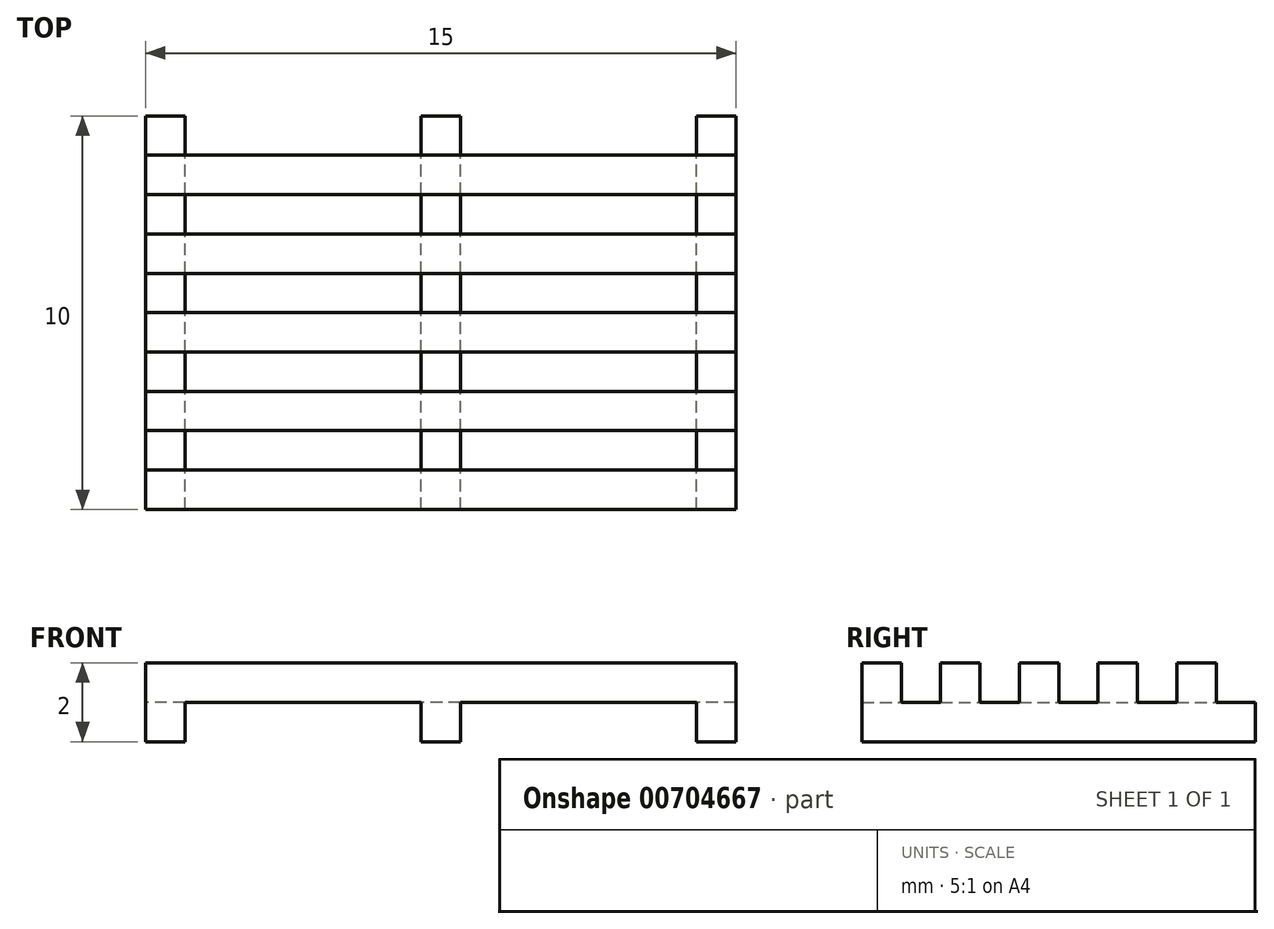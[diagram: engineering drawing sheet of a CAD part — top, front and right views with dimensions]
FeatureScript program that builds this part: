
annotation { "Feature Type Name" : "Feature", "Feature Type Description" : "" }
export const myFeature = defineFeature(function(context is Context, id is Id, definition is map)
    precondition{}
    {
        {
            var Q0;
            Q0=qCreatedBy(makeId("Top.planeOp"),FACE);
            var sketch = newSketch(context, id + "F0", { "sketchPlane" : qUnion([Q0])});
            skLineSegment(sketch, "E0.bottom", {"start": v(0, 0) * mm, "end": v(15, 0) * mm});
            skLineSegment(sketch, "E0.top", {"start": v(0, -10) * mm, "end": v(15, -10) * mm});
            skLineSegment(sketch, "E0.left", {"start": v(0, 0) * mm, "end": v(0, -10) * mm});
            skLineSegment(sketch, "E0.right", {"start": v(15, 0) * mm, "end": v(15, -10) * mm});
            skSolve(sketch);
        }
        {
            var Q0;
            Q0 = qSketchRegion(id + "F0", true);
            extrude(context, id + "F1", {"entities" : qUnion([Q0]), "depth" : 2 * mm, "offsetDistance" : 25 * mm});
        }
        {
            var Q0;
            Q0=qCreatedBy(makeId("Front.planeOp"),FACE);
            var sketch = newSketch(context, id + "F2", { "sketchPlane" : qUnion([Q0])});
            skLineSegment(sketch, "E1", {"start": v(1, 0) * mm, "end": v(1, 1) * mm});
            skLineSegment(sketch, "E2", {"start": v(1, 1) * mm, "end": v(7, 1) * mm});
            skLineSegment(sketch, "E3", {"start": v(7, 1) * mm, "end": v(7, 0) * mm});
            skLineSegment(sketch, "E4", {"start": v(8, 0) * mm, "end": v(8, 1) * mm});
            skLineSegment(sketch, "E5", {"start": v(8, 1) * mm, "end": v(14, 1) * mm});
            skLineSegment(sketch, "E6", {"start": v(14, 1) * mm, "end": v(14, 0) * mm});
            skLineSegment(sketch, "E7", {"start": v(14, 0) * mm, "end": v(8, 0) * mm});
            skLineSegment(sketch, "E8", {"start": v(7, 0) * mm, "end": v(1, 0) * mm});
            skSolve(sketch);
        }
        {
            var Q0;
            Q0 = qSketchRegion(id + "F2", true);
            extrude(context, id + "F3", {"entities" : qUnion([Q0]), "operationType" : NewBodyOperationType.REMOVE, "depth" : 25 * mm, "offsetDistance" : 25 * mm});
        }
        {
            var Q0;
            Q0=makeQuery(id+"F1.opExtrude","SWEPT_FACE",FACE,{"disambiguationData":[OSD([sQuery(id+"F0.wireOp",EDGE,"E0.left")])]});
            var sketch = newSketch(context, id + "F4", { "sketchPlane" : qUnion([Q0])});
            skLineSegment(sketch, "E9", {"start": v(0, 2.24) * mm, "end": v(0, 1) * mm});
            skLineSegment(sketch, "E10", {"start": v(0, 1) * mm, "end": v(1, 1) * mm});
            skLineSegment(sketch, "E11", {"start": v(1, 1) * mm, "end": v(1, 2) * mm});
            skLineSegment(sketch, "E12", {"start": v(1, 2) * mm, "end": v(2, 2) * mm});
            skLineSegment(sketch, "E13", {"start": v(2, 2) * mm, "end": v(2, 1) * mm});
            skLineSegment(sketch, "E14", {"start": v(2, 1) * mm, "end": v(3, 1) * mm});
            skLineSegment(sketch, "E15", {"start": v(3, 1) * mm, "end": v(3, 2) * mm});
            skLineSegment(sketch, "E16", {"start": v(3, 2) * mm, "end": v(4, 2) * mm});
            skLineSegment(sketch, "E17", {"start": v(4, 2) * mm, "end": v(4, 1) * mm});
            skLineSegment(sketch, "E18", {"start": v(4, 1) * mm, "end": v(5, 1) * mm});
            skLineSegment(sketch, "E19", {"start": v(5, 1) * mm, "end": v(5, 2) * mm});
            skLineSegment(sketch, "E20", {"start": v(5, 2) * mm, "end": v(6, 2) * mm});
            skLineSegment(sketch, "E21", {"start": v(6, 2) * mm, "end": v(6, 1) * mm});
            skLineSegment(sketch, "E22", {"start": v(6, 1) * mm, "end": v(7, 1) * mm});
            skLineSegment(sketch, "E23", {"start": v(7, 1) * mm, "end": v(7, 2) * mm});
            skLineSegment(sketch, "E24", {"start": v(7, 2) * mm, "end": v(8, 2) * mm});
            skLineSegment(sketch, "E25", {"start": v(8, 2) * mm, "end": v(8, 1) * mm});
            skLineSegment(sketch, "E26", {"start": v(8, 1) * mm, "end": v(9, 1) * mm});
            skLineSegment(sketch, "E27", {"start": v(9, 1) * mm, "end": v(9, 2) * mm});
            skLineSegment(sketch, "E28", {"start": v(9, 2) * mm, "end": v(10, 2) * mm});
            skLineSegment(sketch, "E29", {"start": v(10, 2) * mm, "end": v(10, 1) * mm});
            skLineSegment(sketch, "E30", {"start": v(10, 1) * mm, "end": v(10.68, 1) * mm});
            skLineSegment(sketch, "E31", {"start": v(10.68, 1) * mm, "end": v(10.68, 3.5) * mm});
            skLineSegment(sketch, "E32", {"start": v(10.68, 3.5) * mm, "end": v(0, 3.5) * mm});
            skLineSegment(sketch, "E33", {"start": v(0, 3.5) * mm, "end": v(0, 2.24) * mm});
            skSolve(sketch);
        }
        {
            var Q0;
            Q0 = qSketchRegion(id + "F4", true);
            extrude(context, id + "F5", {"entities" : qUnion([Q0]), "operationType" : NewBodyOperationType.REMOVE, "oppositeDirection" : true, "depth" : 25 * mm, "offsetDistance" : 25 * mm});
        }
    });
